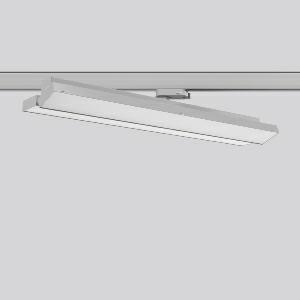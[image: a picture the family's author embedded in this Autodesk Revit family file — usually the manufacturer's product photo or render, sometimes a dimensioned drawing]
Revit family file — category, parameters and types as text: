
# Revit family: tx-move_742164_004_1_b0c1
name_source: partatom
category: Lighting Fixtures
units: mm (PartAtom-declared; Revit-internal decimal feet)

## family parameters
Cut with Voids When Loaded = No
Host = Face
Light Source = No
Part Type = Normal
Room Calculation Point = No
Round Connector Dimension = Use Diameter
Shared = No

## types (1)
- MultiLumen 1 (1 x LED Modul 840, 2625 lm, 4000)
    Apparent Load = 41 VA
    CIE Flux Codes = 47 79 96 100 100
    Color Rendering = 80
    Color Temperature = 4000
    Default Elevation = 1800 mm
    Description = Series: TX-MOVE
Multifunctional surface-mounted spotlight for area lighting. Very flat design. Housing: sheet steel, powder-coated. Rotation range: 356°. Swivel range: 90°. Consistent alignment possible with visible tilt scale. High-efficiency LED units with flush-mounted opal diffuser made of non-yellowing PMMA. Symmetrical wide beam light emission. With multi adaptor for 3-circuit tracks 230 V. Suitable for Track on ceiling. MultiLumen: Luminous flux adjustable in 3 steps. Factory setting is the highest luminous flux. Environmentally friendly and resource-saving due to replaceable and recyclable components. 
Colour: silver, matt (approx. RAL 9006)
Length: 570 mm
Width: 119 mm
Height: 92 mm
Lamp: LED
Socket: without socket
Colour temperature: 4000K
Colour rendering index (CRI): 80
System power: 41 W
Rated luminous flux: 5250 lm
Luminous efficiency: 128 lm/W
System power 2: 57 W
Rated luminous flux 2: 7150 lm
Luminous efficiency 2: 125 lm/W
System power 3: 73 W
Rated luminous flux 3: 8750 lm
Luminous efficiency 3: 120 lm/W
Control gear: Regulated power supply
Protection class: I
Type of protection: IP 20
    Height = 75 mm
    Lamp = 1 x LED Modul 840
    Lamp Light Flux = 2625 lm
    Lamp count = 1
    Length = 569 mm
    Lifetime = 50000 h
    Luminous efficacy = 128 lm/W
    Manufacturer = RZB
    ModVariant = No
    Model = 742164.004.1
    Mounting Place = Ceiling
    Mounting Type = Surface mounted
    Number of Poles = 1
    OnlyDefault = Yes
    Power Factor = 1
    Product Name = TX-MOVE
    Product group = Track mounted projectors
    ProductGroupID = 301
    Protection Class = Protection class I
    Protection Degree = IP 20
    RLX_Detail_Level = 1
    RLX_Emergency_Light_Flux = 0 lm
    RLX_Emergency_Type = 0
    RLX_Emergency_Type_DB = No
    RlxData = <blob elided: 32269 chars, md5=8cd6884d>
    Socket = socket
    Standby Power = 0 W
    System Light Flux = 5250 lm
    System Power = 41 W
    Type Comments = MultiLumen 1
    Type Image = 742164.004.jpg
    URL = http://relux.com
    VarID = multilumen_1
    Voltage = 0 V
    Weight = 0.00 kg
    Width = 119 mm

## geometry (parser evidence)
native form markers: Blend x4, Sweep x16
no freeform markers — native parametric forms only
